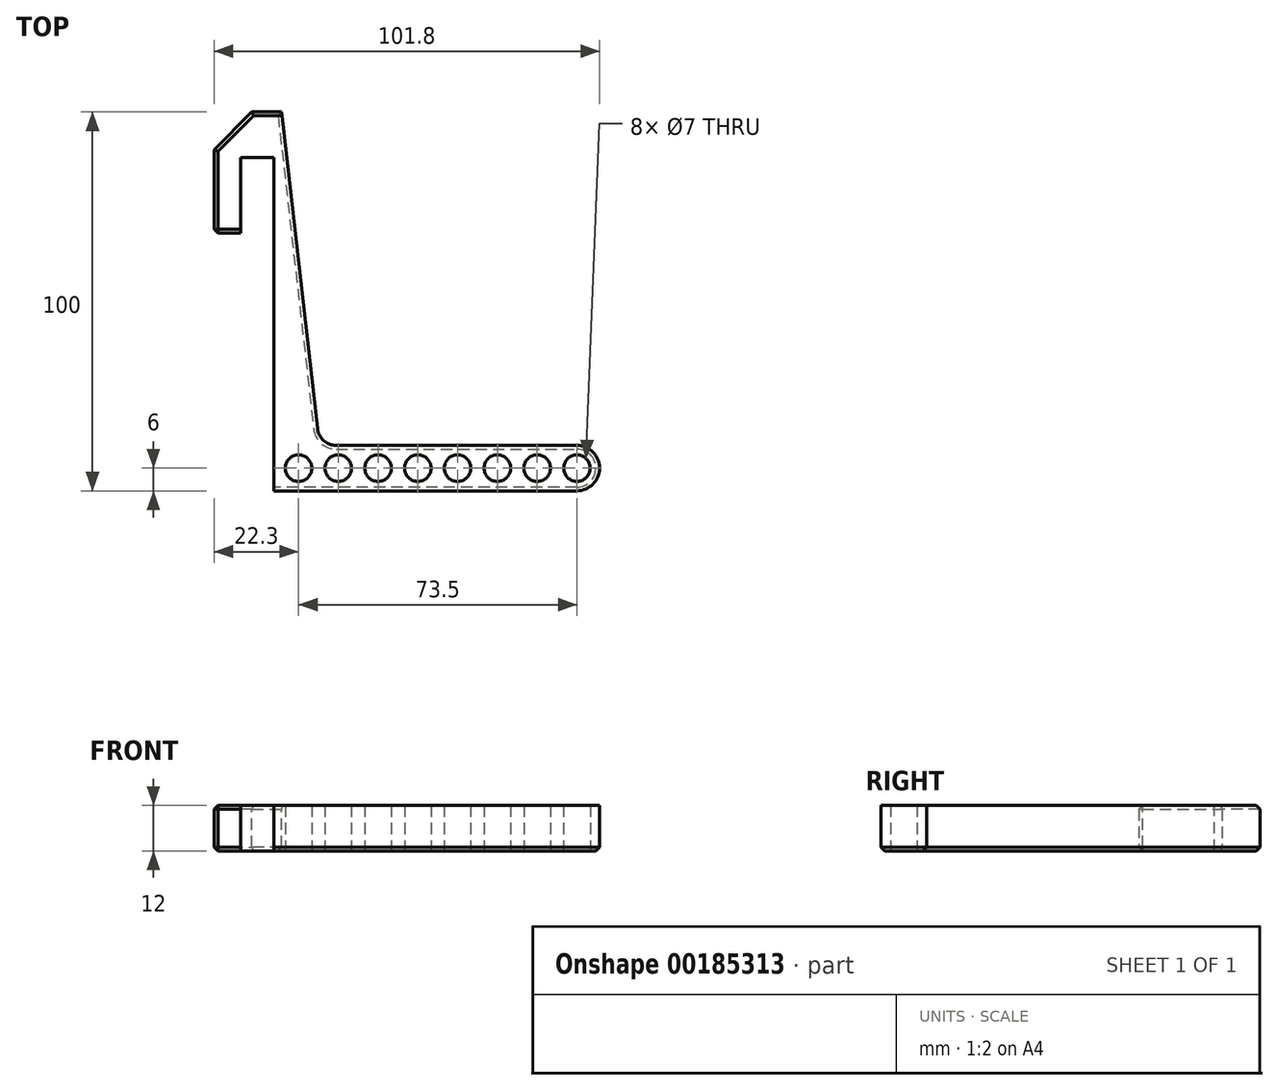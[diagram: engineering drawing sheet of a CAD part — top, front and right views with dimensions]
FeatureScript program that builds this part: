
annotation { "Feature Type Name" : "Feature", "Feature Type Description" : "" }
export const myFeature = defineFeature(function(context is Context, id is Id, definition is map)
    precondition{}
    {
        {
            var Q0;
            Q0=qCreatedBy(makeId("Top.planeOp"),FACE);
            var sketch = newSketch(context, id + "F0", { "sketchPlane" : qUnion([Q0])});
            skLineSegment(sketch, "E0.bottom", {"start": v(0, 100) * mm, "end": v(12, 100) * mm});
            skLineSegment(sketch, "E0.left", {"start": v(0, 100) * mm, "end": v(0, 0) * mm});
            skLineSegment(sketch, "E0.right", {"start": v(12, 100) * mm, "end": v(12, 12) * mm});
            skLineSegment(sketch, "E1.bottom", {"start": v(0, 0) * mm, "end": v(80, 0) * mm});
            skLineSegment(sketch, "E1.top", {"start": v(12, 12) * mm, "end": v(80, 12) * mm});
            skArc(sketch, "E2", {"start": v(80, 0) * mm, "mid": v(86, 6) * mm, "end": v(80, 12) * mm});
            skCircle(sketch, "E3.cCircle", {"center": v(80, 6) * mm, "radius": 3.5 * mm});
            skCircle(sketch, "E4.1.0.0", {"center": v(69.5, 6) * mm, "radius": 3.5 * mm});
            skCircle(sketch, "E4.2.0.0", {"center": v(59, 6) * mm, "radius": 3.5 * mm});
            skCircle(sketch, "E4.3.0.0", {"center": v(48.5, 6) * mm, "radius": 3.5 * mm});
            skCircle(sketch, "E4.4.0.0", {"center": v(38, 6) * mm, "radius": 3.5 * mm});
            skCircle(sketch, "E4.5.0.0", {"center": v(27.5, 6) * mm, "radius": 3.5 * mm});
            skCircle(sketch, "E4.6.0.0", {"center": v(17, 6) * mm, "radius": 3.5 * mm});
            skCircle(sketch, "E4.7.0.0", {"center": v(6.5, 6) * mm, "radius": 3.5 * mm});
            skLineSegment(sketch, "E4.direction1", {"start": v(80, 6) * mm, "end": v(69.5, 6) * mm, "construction": true});
            skSolve(sketch);
        }
        {
            var Q0;
            Q0=qSketchRegion(id+"F0",true);
            extrude(context, id + "F1", {"entities" : qUnion([Q0]), "depth" : 12 * mm});
        }
        {
            var Q0;
            Q0=makeQuery(id+"F1.opExtrude","CAP_FACE",FACE,{"disambiguationData":[OSD([sQuery(id+"F0.wireOp",EDGE,"E0.bottom"),sQuery(id+"F0.wireOp",EDGE,"E0.left"),sQuery(id+"F0.wireOp",EDGE,"E0.right"),sQuery(id+"F0.wireOp",EDGE,"E1.bottom"),sQuery(id+"F0.wireOp",EDGE,"E1.top"),sQuery(id+"F0.wireOp",EDGE,"E2"),sQuery(id+"F0.wireOp",EDGE,"E3.0"),sQuery(id+"F0.wireOp",EDGE,"E3.1"),sQuery(id+"F0.wireOp",EDGE,"E3.2"),sQuery(id+"F0.wireOp",EDGE,"E3.3"),sQuery(id+"F0.wireOp",EDGE,"E3.4"),sQuery(id+"F0.wireOp",EDGE,"E3.5"),sQuery(id+"F0.wireOp",EDGE,"ffaec4ea-79df-4dc1-b443-eba8a6825352.1.0.0"),sQuery(id+"F0.wireOp",EDGE,"ffaec4ea-79df-4dc1-b443-eba8a6825352.1.0.1"),sQuery(id+"F0.wireOp",EDGE,"ffaec4ea-79df-4dc1-b443-eba8a6825352.1.0.2"),sQuery(id+"F0.wireOp",EDGE,"ffaec4ea-79df-4dc1-b443-eba8a6825352.1.0.3"),sQuery(id+"F0.wireOp",EDGE,"ffaec4ea-79df-4dc1-b443-eba8a6825352.1.0.4"),sQuery(id+"F0.wireOp",EDGE,"ffaec4ea-79df-4dc1-b443-eba8a6825352.1.0.5"),sQuery(id+"F0.wireOp",EDGE,"ffaec4ea-79df-4dc1-b443-eba8a6825352.2.0.0"),sQuery(id+"F0.wireOp",EDGE,"ffaec4ea-79df-4dc1-b443-eba8a6825352.2.0.1"),sQuery(id+"F0.wireOp",EDGE,"ffaec4ea-79df-4dc1-b443-eba8a6825352.2.0.2"),sQuery(id+"F0.wireOp",EDGE,"ffaec4ea-79df-4dc1-b443-eba8a6825352.2.0.3"),sQuery(id+"F0.wireOp",EDGE,"ffaec4ea-79df-4dc1-b443-eba8a6825352.2.0.4"),sQuery(id+"F0.wireOp",EDGE,"ffaec4ea-79df-4dc1-b443-eba8a6825352.2.0.5"),sQuery(id+"F0.wireOp",EDGE,"ffaec4ea-79df-4dc1-b443-eba8a6825352.3.0.0"),sQuery(id+"F0.wireOp",EDGE,"ffaec4ea-79df-4dc1-b443-eba8a6825352.3.0.1"),sQuery(id+"F0.wireOp",EDGE,"ffaec4ea-79df-4dc1-b443-eba8a6825352.3.0.2"),sQuery(id+"F0.wireOp",EDGE,"ffaec4ea-79df-4dc1-b443-eba8a6825352.3.0.3"),sQuery(id+"F0.wireOp",EDGE,"ffaec4ea-79df-4dc1-b443-eba8a6825352.3.0.4"),sQuery(id+"F0.wireOp",EDGE,"ffaec4ea-79df-4dc1-b443-eba8a6825352.3.0.5"),sQuery(id+"F0.wireOp",EDGE,"ffaec4ea-79df-4dc1-b443-eba8a6825352.4.0.0"),sQuery(id+"F0.wireOp",EDGE,"ffaec4ea-79df-4dc1-b443-eba8a6825352.4.0.1"),sQuery(id+"F0.wireOp",EDGE,"ffaec4ea-79df-4dc1-b443-eba8a6825352.4.0.2"),sQuery(id+"F0.wireOp",EDGE,"ffaec4ea-79df-4dc1-b443-eba8a6825352.4.0.3"),sQuery(id+"F0.wireOp",EDGE,"ffaec4ea-79df-4dc1-b443-eba8a6825352.4.0.4"),sQuery(id+"F0.wireOp",EDGE,"ffaec4ea-79df-4dc1-b443-eba8a6825352.4.0.5"),sQuery(id+"F0.wireOp",EDGE,"ffaec4ea-79df-4dc1-b443-eba8a6825352.5.0.0"),sQuery(id+"F0.wireOp",EDGE,"ffaec4ea-79df-4dc1-b443-eba8a6825352.5.0.1"),sQuery(id+"F0.wireOp",EDGE,"ffaec4ea-79df-4dc1-b443-eba8a6825352.5.0.2"),sQuery(id+"F0.wireOp",EDGE,"ffaec4ea-79df-4dc1-b443-eba8a6825352.5.0.3"),sQuery(id+"F0.wireOp",EDGE,"ffaec4ea-79df-4dc1-b443-eba8a6825352.5.0.4"),sQuery(id+"F0.wireOp",EDGE,"ffaec4ea-79df-4dc1-b443-eba8a6825352.5.0.5"),sQuery(id+"F0.wireOp",EDGE,"ffaec4ea-79df-4dc1-b443-eba8a6825352.6.0.0"),sQuery(id+"F0.wireOp",EDGE,"ffaec4ea-79df-4dc1-b443-eba8a6825352.6.0.1"),sQuery(id+"F0.wireOp",EDGE,"ffaec4ea-79df-4dc1-b443-eba8a6825352.6.0.2"),sQuery(id+"F0.wireOp",EDGE,"ffaec4ea-79df-4dc1-b443-eba8a6825352.6.0.3"),sQuery(id+"F0.wireOp",EDGE,"ffaec4ea-79df-4dc1-b443-eba8a6825352.6.0.4"),sQuery(id+"F0.wireOp",EDGE,"ffaec4ea-79df-4dc1-b443-eba8a6825352.6.0.5"),sQuery(id+"F0.wireOp",EDGE,"ffaec4ea-79df-4dc1-b443-eba8a6825352.7.0.0"),sQuery(id+"F0.wireOp",EDGE,"ffaec4ea-79df-4dc1-b443-eba8a6825352.7.0.1"),sQuery(id+"F0.wireOp",EDGE,"ffaec4ea-79df-4dc1-b443-eba8a6825352.7.0.2"),sQuery(id+"F0.wireOp",EDGE,"ffaec4ea-79df-4dc1-b443-eba8a6825352.7.0.3"),sQuery(id+"F0.wireOp",EDGE,"ffaec4ea-79df-4dc1-b443-eba8a6825352.7.0.4"),sQuery(id+"F0.wireOp",EDGE,"ffaec4ea-79df-4dc1-b443-eba8a6825352.7.0.5")])],"isStart":false});
            var sketch = newSketch(context, id + "F2", { "sketchPlane" : qUnion([Q0])});
            skLineSegment(sketch, "E5", {"start": v(12, 12) * mm, "end": v(2, 100) * mm});
            skLineSegment(sketch, "E6", {"start": v(12, 12) * mm, "end": v(12, 100) * mm});
            skLineSegment(sketch, "E7", {"start": v(12, 100) * mm, "end": v(2, 100) * mm});
            skSolve(sketch);
        }
        {
            var Q0;
            Q0=qSketchRegion(id+"F2",true);
            extrude(context, id + "F3", {"entities" : qUnion([Q0]), "operationType" : NewBodyOperationType.REMOVE, "oppositeDirection" : true, "depth" : 25 * mm});
        }
        {
            var Q0;
            {var subQ0=sQuery(id+"F0.wireOp",EDGE,"E1.top");Q0=makeQuery(id+"F3.boolean.opBoolean","MERGE",EDGE,{"derivedFrom":[makeQuery(id+"F1.opExtrude","SWEPT_EDGE",EDGE,{"disambiguationData":[OSD([sQuery(id+"F0.wireOp",EDGE,"E0.right"),subQ0])]}),makeQuery(id+"F3.opExtrude","SWEPT_EDGE",EDGE,{"disambiguationData":[OSD([subQ0,sQuery(id+"F2.wireOp",EDGE,"E5"),sQuery(id+"F2.wireOp",EDGE,"E6")])]})]});}
            fillet(context, id + "F4", {"entities" : qUnion([Q0]), "radius" : 5 * mm, "tangentPropagation" : true, "allowEdgeOverflow" : false});
        }
        {
            var Q0;
            Q0=makeQuery(id+"F1.opExtrude","SWEPT_FACE",FACE,{"disambiguationData":[OSD([sQuery(id+"F0.wireOp",EDGE,"E0.left")])]});
            var sketch = newSketch(context, id + "F5", { "sketchPlane" : qUnion([Q0])});
            skLineSegment(sketch, "E8.bottom", {"start": v(-100, 0) * mm, "end": v(-88, 0) * mm});
            skLineSegment(sketch, "E8.top", {"start": v(-100, 12) * mm, "end": v(-88, 12) * mm});
            skLineSegment(sketch, "E8.left", {"start": v(-100, 0) * mm, "end": v(-100, 12) * mm});
            skLineSegment(sketch, "E8.right", {"start": v(-88, 0) * mm, "end": v(-88, 12) * mm});
            skSolve(sketch);
        }
        {
            var Q0;
            Q0 = qSketchRegion(id + "F5", true);
            extrude(context, id + "F6", {"entities" : qUnion([Q0]), "operationType" : NewBodyOperationType.ADD, "depth" : 15.8 * mm});
        }
        {
            var Q0;
            Q0=makeQuery(id+"F6.opExtrude","SWEPT_FACE",FACE,{"disambiguationData":[OSD([sQuery(id+"F5.wireOp",EDGE,"E8.right")])]});
            var sketch = newSketch(context, id + "F7", { "sketchPlane" : qUnion([Q0])});
            skLineSegment(sketch, "E9.bottom", {"start": v(-15.8, 12) * mm, "end": v(-8.8, 12) * mm});
            skLineSegment(sketch, "E9.top", {"start": v(-15.8, 0) * mm, "end": v(-8.8, 0) * mm});
            skLineSegment(sketch, "E9.left", {"start": v(-15.8, 12) * mm, "end": v(-15.8, 0) * mm});
            skLineSegment(sketch, "E9.right", {"start": v(-8.8, 12) * mm, "end": v(-8.8, 0) * mm});
            skSolve(sketch);
        }
        {
            var Q0;
            Q0 = qSketchRegion(id + "F7", true);
            extrude(context, id + "F8", {"entities" : qUnion([Q0]), "operationType" : NewBodyOperationType.ADD, "depth" : 20 * mm});
        }
        {
            var Q0;
            Q0=makeQuery(id+"F6.opExtrude","CAP_EDGE",EDGE,{"disambiguationData":[OSD([sQuery(id+"F5.wireOp",EDGE,"E8.left")])],"isStart":false});
            chamfer(context, id + "F9", {"entities" : qUnion([Q0]), "width" : 10 * mm, "tangentPropagation" : true});
        }
        {
            var Q0;
            Q0=makeQuery(id+"F3.boolean.opBoolean","COPY",EDGE,{"derivedFrom":makeQuery(id+"F3.opExtrude","CAP_EDGE",EDGE,{"disambiguationData":[OSD([sQuery(id+"F2.wireOp",EDGE,"E5")])],"isStart":true})});
            var Q1;
            Q1=makeQuery(id+"F3.boolean.opBoolean","INTERSECT",EDGE,{"derivedFrom":[makeQuery(id+"F1.opExtrude","CAP_FACE",FACE,{"disambiguationData":[OSD([sQuery(id+"F0.wireOp",EDGE,"E0.bottom"),sQuery(id+"F0.wireOp",EDGE,"E0.left"),sQuery(id+"F0.wireOp",EDGE,"E0.right"),sQuery(id+"F0.wireOp",EDGE,"E1.bottom"),sQuery(id+"F0.wireOp",EDGE,"E1.top"),sQuery(id+"F0.wireOp",EDGE,"E2"),sQuery(id+"F0.wireOp",EDGE,"E3.cCircle"),sQuery(id+"F0.wireOp",EDGE,"E4.1.0.0"),sQuery(id+"F0.wireOp",EDGE,"E4.2.0.0"),sQuery(id+"F0.wireOp",EDGE,"E4.3.0.0"),sQuery(id+"F0.wireOp",EDGE,"E4.4.0.0"),sQuery(id+"F0.wireOp",EDGE,"E4.5.0.0"),sQuery(id+"F0.wireOp",EDGE,"E4.6.0.0"),sQuery(id+"F0.wireOp",EDGE,"E4.7.0.0")])],"isStart":true}),makeQuery(id+"F3.opExtrude","SWEPT_FACE",FACE,{"disambiguationData":[OSD([sQuery(id+"F2.wireOp",EDGE,"E5")])]})]});
            var Q2;
            Q2=makeQuery(id+"F6.boolean.opBoolean","MERGE",EDGE,{"derivedFrom":[makeQuery(id+"F1.opExtrude","CAP_EDGE",EDGE,{"disambiguationData":[OSD([sQuery(id+"F0.wireOp",EDGE,"E0.bottom")])],"isStart":false}),makeQuery(id+"F6.opExtrude","SWEPT_EDGE",EDGE,{"disambiguationData":[OSD([sQuery(id+"F5.wireOp",EDGE,"E8.top"),sQuery(id+"F5.wireOp",EDGE,"E8.left")])]})]});
            var Q3;
            Q3=makeQuery(id+"F9.opChamfer","BLEND_EDGE",EDGE,{"blendedFrom":[makeQuery(id+"F6.opExtrude","CAP_EDGE",EDGE,{"disambiguationData":[OSD([sQuery(id+"F5.wireOp",EDGE,"E8.left")])],"isStart":false}),makeQuery(id+"F8.boolean.opBoolean","MERGE",FACE,{"derivedFrom":[makeQuery(id+"F6.boolean.opBoolean","MERGE",FACE,{"derivedFrom":[makeQuery(id+"F1.opExtrude","CAP_FACE",FACE,{"disambiguationData":[OSD([sQuery(id+"F0.wireOp",EDGE,"E0.bottom"),sQuery(id+"F0.wireOp",EDGE,"E0.left"),sQuery(id+"F0.wireOp",EDGE,"E0.right"),sQuery(id+"F0.wireOp",EDGE,"E1.bottom"),sQuery(id+"F0.wireOp",EDGE,"E1.top"),sQuery(id+"F0.wireOp",EDGE,"E2"),sQuery(id+"F0.wireOp",EDGE,"E3.cCircle"),sQuery(id+"F0.wireOp",EDGE,"E4.1.0.0"),sQuery(id+"F0.wireOp",EDGE,"E4.2.0.0"),sQuery(id+"F0.wireOp",EDGE,"E4.3.0.0"),sQuery(id+"F0.wireOp",EDGE,"E4.4.0.0"),sQuery(id+"F0.wireOp",EDGE,"E4.5.0.0"),sQuery(id+"F0.wireOp",EDGE,"E4.6.0.0"),sQuery(id+"F0.wireOp",EDGE,"E4.7.0.0")])],"isStart":false}),makeQuery(id+"F6.opExtrude","SWEPT_FACE",FACE,{"disambiguationData":[OSD([sQuery(id+"F5.wireOp",EDGE,"E8.top")])]})]}),makeQuery(id+"F8.opExtrude","SWEPT_FACE",FACE,{"disambiguationData":[OSD([sQuery(id+"F7.wireOp",EDGE,"E9.bottom")])]})]})],"blendedInto":[makeQuery(id+"F8.boolean.opBoolean","MERGE",FACE,{"derivedFrom":[makeQuery(id+"F6.boolean.opBoolean","MERGE",FACE,{"derivedFrom":[makeQuery(id+"F1.opExtrude","CAP_FACE",FACE,{"disambiguationData":[OSD([sQuery(id+"F0.wireOp",EDGE,"E0.bottom"),sQuery(id+"F0.wireOp",EDGE,"E0.left"),sQuery(id+"F0.wireOp",EDGE,"E0.right"),sQuery(id+"F0.wireOp",EDGE,"E1.bottom"),sQuery(id+"F0.wireOp",EDGE,"E1.top"),sQuery(id+"F0.wireOp",EDGE,"E2"),sQuery(id+"F0.wireOp",EDGE,"E3.cCircle"),sQuery(id+"F0.wireOp",EDGE,"E4.1.0.0"),sQuery(id+"F0.wireOp",EDGE,"E4.2.0.0"),sQuery(id+"F0.wireOp",EDGE,"E4.3.0.0"),sQuery(id+"F0.wireOp",EDGE,"E4.4.0.0"),sQuery(id+"F0.wireOp",EDGE,"E4.5.0.0"),sQuery(id+"F0.wireOp",EDGE,"E4.6.0.0"),sQuery(id+"F0.wireOp",EDGE,"E4.7.0.0")])],"isStart":false}),makeQuery(id+"F6.opExtrude","SWEPT_FACE",FACE,{"disambiguationData":[OSD([sQuery(id+"F5.wireOp",EDGE,"E8.top")])]})]}),makeQuery(id+"F8.opExtrude","SWEPT_FACE",FACE,{"disambiguationData":[OSD([sQuery(id+"F7.wireOp",EDGE,"E9.bottom")])]})]})]});
            var Q4;
            Q4=makeQuery(id+"F8.boolean.opBoolean","MERGE",EDGE,{"derivedFrom":[makeQuery(id+"F6.opExtrude","CAP_EDGE",EDGE,{"disambiguationData":[OSD([sQuery(id+"F5.wireOp",EDGE,"E8.top")])],"isStart":false}),makeQuery(id+"F8.opExtrude","SWEPT_EDGE",EDGE,{"disambiguationData":[OSD([sQuery(id+"F7.wireOp",EDGE,"E9.bottom"),sQuery(id+"F7.wireOp",EDGE,"E9.left")])]})]});
            var Q5;
            Q5=makeQuery(id+"F6.boolean.opBoolean","MERGE",EDGE,{"derivedFrom":[makeQuery(id+"F1.opExtrude","CAP_EDGE",EDGE,{"disambiguationData":[OSD([sQuery(id+"F0.wireOp",EDGE,"E0.bottom")])],"isStart":true}),makeQuery(id+"F6.opExtrude","SWEPT_EDGE",EDGE,{"disambiguationData":[OSD([sQuery(id+"F5.wireOp",EDGE,"E8.bottom"),sQuery(id+"F5.wireOp",EDGE,"E8.left")])]})]});
            var Q6;
            Q6=makeQuery(id+"F9.opChamfer","BLEND_EDGE",EDGE,{"blendedFrom":[makeQuery(id+"F6.opExtrude","CAP_EDGE",EDGE,{"disambiguationData":[OSD([sQuery(id+"F5.wireOp",EDGE,"E8.left")])],"isStart":false}),makeQuery(id+"F8.boolean.opBoolean","MERGE",FACE,{"derivedFrom":[makeQuery(id+"F6.boolean.opBoolean","MERGE",FACE,{"derivedFrom":[makeQuery(id+"F1.opExtrude","CAP_FACE",FACE,{"disambiguationData":[OSD([sQuery(id+"F0.wireOp",EDGE,"E0.bottom"),sQuery(id+"F0.wireOp",EDGE,"E0.left"),sQuery(id+"F0.wireOp",EDGE,"E0.right"),sQuery(id+"F0.wireOp",EDGE,"E1.bottom"),sQuery(id+"F0.wireOp",EDGE,"E1.top"),sQuery(id+"F0.wireOp",EDGE,"E2"),sQuery(id+"F0.wireOp",EDGE,"E3.cCircle"),sQuery(id+"F0.wireOp",EDGE,"E4.1.0.0"),sQuery(id+"F0.wireOp",EDGE,"E4.2.0.0"),sQuery(id+"F0.wireOp",EDGE,"E4.3.0.0"),sQuery(id+"F0.wireOp",EDGE,"E4.4.0.0"),sQuery(id+"F0.wireOp",EDGE,"E4.5.0.0"),sQuery(id+"F0.wireOp",EDGE,"E4.6.0.0"),sQuery(id+"F0.wireOp",EDGE,"E4.7.0.0")])],"isStart":true}),makeQuery(id+"F6.opExtrude","SWEPT_FACE",FACE,{"disambiguationData":[OSD([sQuery(id+"F5.wireOp",EDGE,"E8.bottom")])]})]}),makeQuery(id+"F8.opExtrude","SWEPT_FACE",FACE,{"disambiguationData":[OSD([sQuery(id+"F7.wireOp",EDGE,"E9.top")])]})]})],"blendedInto":[makeQuery(id+"F8.boolean.opBoolean","MERGE",FACE,{"derivedFrom":[makeQuery(id+"F6.boolean.opBoolean","MERGE",FACE,{"derivedFrom":[makeQuery(id+"F1.opExtrude","CAP_FACE",FACE,{"disambiguationData":[OSD([sQuery(id+"F0.wireOp",EDGE,"E0.bottom"),sQuery(id+"F0.wireOp",EDGE,"E0.left"),sQuery(id+"F0.wireOp",EDGE,"E0.right"),sQuery(id+"F0.wireOp",EDGE,"E1.bottom"),sQuery(id+"F0.wireOp",EDGE,"E1.top"),sQuery(id+"F0.wireOp",EDGE,"E2"),sQuery(id+"F0.wireOp",EDGE,"E3.cCircle"),sQuery(id+"F0.wireOp",EDGE,"E4.1.0.0"),sQuery(id+"F0.wireOp",EDGE,"E4.2.0.0"),sQuery(id+"F0.wireOp",EDGE,"E4.3.0.0"),sQuery(id+"F0.wireOp",EDGE,"E4.4.0.0"),sQuery(id+"F0.wireOp",EDGE,"E4.5.0.0"),sQuery(id+"F0.wireOp",EDGE,"E4.6.0.0"),sQuery(id+"F0.wireOp",EDGE,"E4.7.0.0")])],"isStart":true}),makeQuery(id+"F6.opExtrude","SWEPT_FACE",FACE,{"disambiguationData":[OSD([sQuery(id+"F5.wireOp",EDGE,"E8.bottom")])]})]}),makeQuery(id+"F8.opExtrude","SWEPT_FACE",FACE,{"disambiguationData":[OSD([sQuery(id+"F7.wireOp",EDGE,"E9.top")])]})]})]});
            var Q7;
            Q7=makeQuery(id+"F8.boolean.opBoolean","MERGE",EDGE,{"derivedFrom":[makeQuery(id+"F6.opExtrude","CAP_EDGE",EDGE,{"disambiguationData":[OSD([sQuery(id+"F5.wireOp",EDGE,"E8.bottom")])],"isStart":false}),makeQuery(id+"F8.opExtrude","SWEPT_EDGE",EDGE,{"disambiguationData":[OSD([sQuery(id+"F7.wireOp",EDGE,"E9.top"),sQuery(id+"F7.wireOp",EDGE,"E9.left")])]})]});
            var Q8;
            Q8=makeQuery(id+"F8.opExtrude","CAP_EDGE",EDGE,{"disambiguationData":[OSD([sQuery(id+"F7.wireOp",EDGE,"E9.left")])],"isStart":false});
            var Q9;
            Q9=makeQuery(id+"F8.opExtrude","CAP_EDGE",EDGE,{"disambiguationData":[OSD([sQuery(id+"F7.wireOp",EDGE,"E9.bottom")])],"isStart":false});
            var Q10;
            Q10=makeQuery(id+"F8.opExtrude","CAP_EDGE",EDGE,{"disambiguationData":[OSD([sQuery(id+"F7.wireOp",EDGE,"E9.top")])],"isStart":false});
            chamfer(context, id + "F10", {"entities" : qUnion([Q0, Q1, Q2, Q3, Q4, Q5, Q6, Q7, Q8, Q9, Q10]), "width" : 1 * mm, "tangentPropagation" : true});
        }
    });
